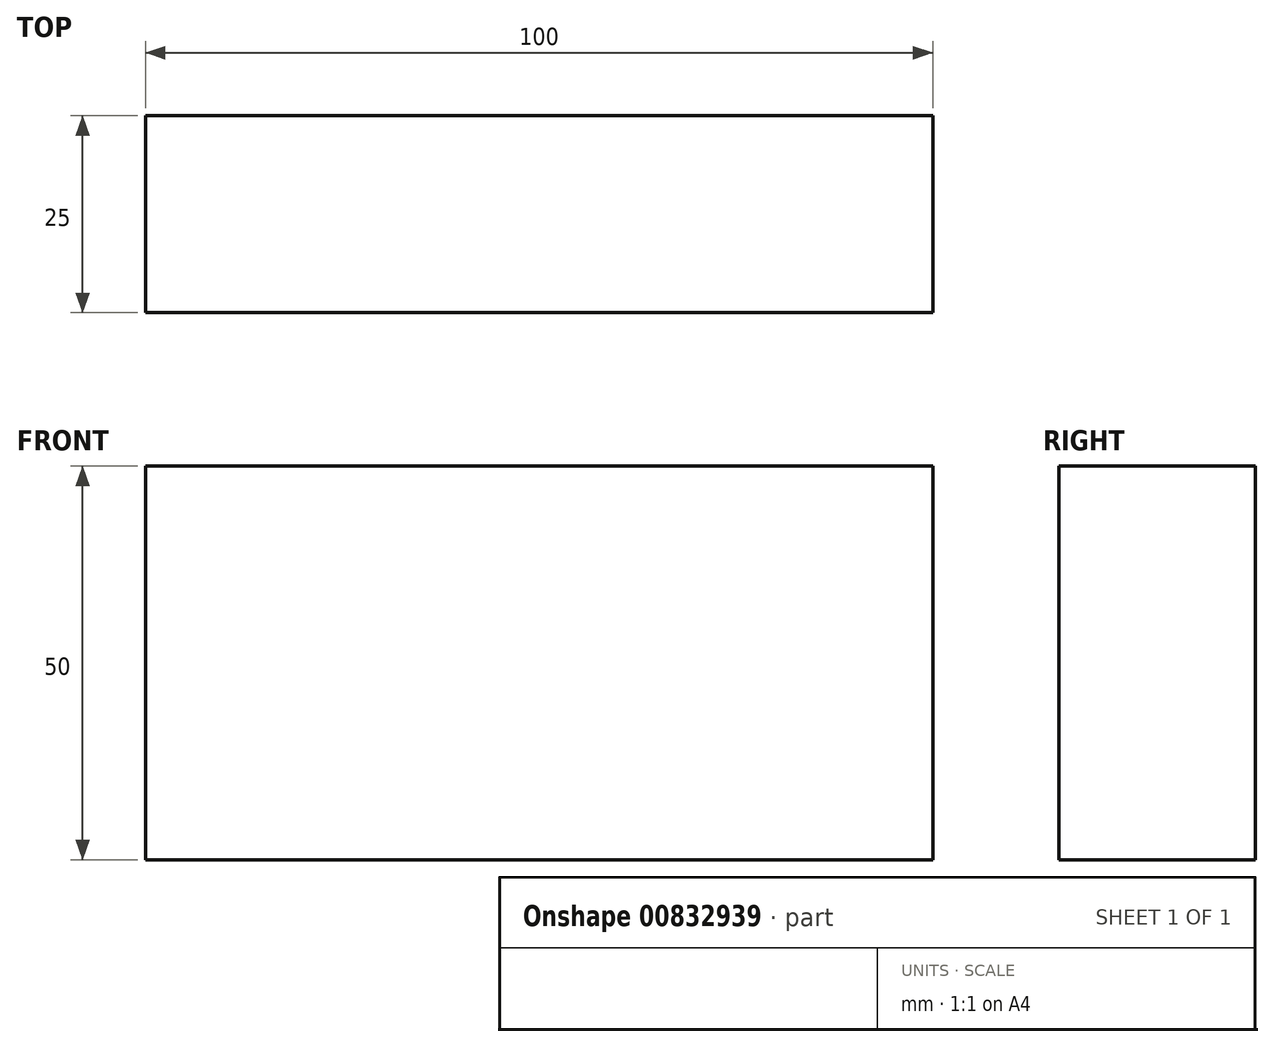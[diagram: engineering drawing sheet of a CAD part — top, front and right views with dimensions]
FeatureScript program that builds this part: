
annotation { "Feature Type Name" : "Feature", "Feature Type Description" : "" }
export const myFeature = defineFeature(function(context is Context, id is Id, definition is map)
    precondition{}
    {
        {
            var Q0;
            Q0=qCreatedBy(makeId("Front.planeOp"),FACE);
            var sketch = newSketch(context, id + "F0", { "sketchPlane" : qUnion([Q0])});
            skLineSegment(sketch, "E0.bottom", {"start": v(-50, 25) * mm, "end": v(50, 25) * mm});
            skLineSegment(sketch, "E0.top", {"start": v(-50, -25) * mm, "end": v(50, -25) * mm});
            skLineSegment(sketch, "E0.left", {"start": v(-50, 25) * mm, "end": v(-50, -25) * mm});
            skLineSegment(sketch, "E0.right", {"start": v(50, 25) * mm, "end": v(50, -25) * mm});
            skSolve(sketch);
        }
        {
            var Q0;
            Q0 = qSketchRegion(id + "F0", true);
            extrude(context, id + "F1", {"entities" : qUnion([Q0]), "depth" : 25 * mm, "offsetDistance" : 25 * mm});
        }
    });
